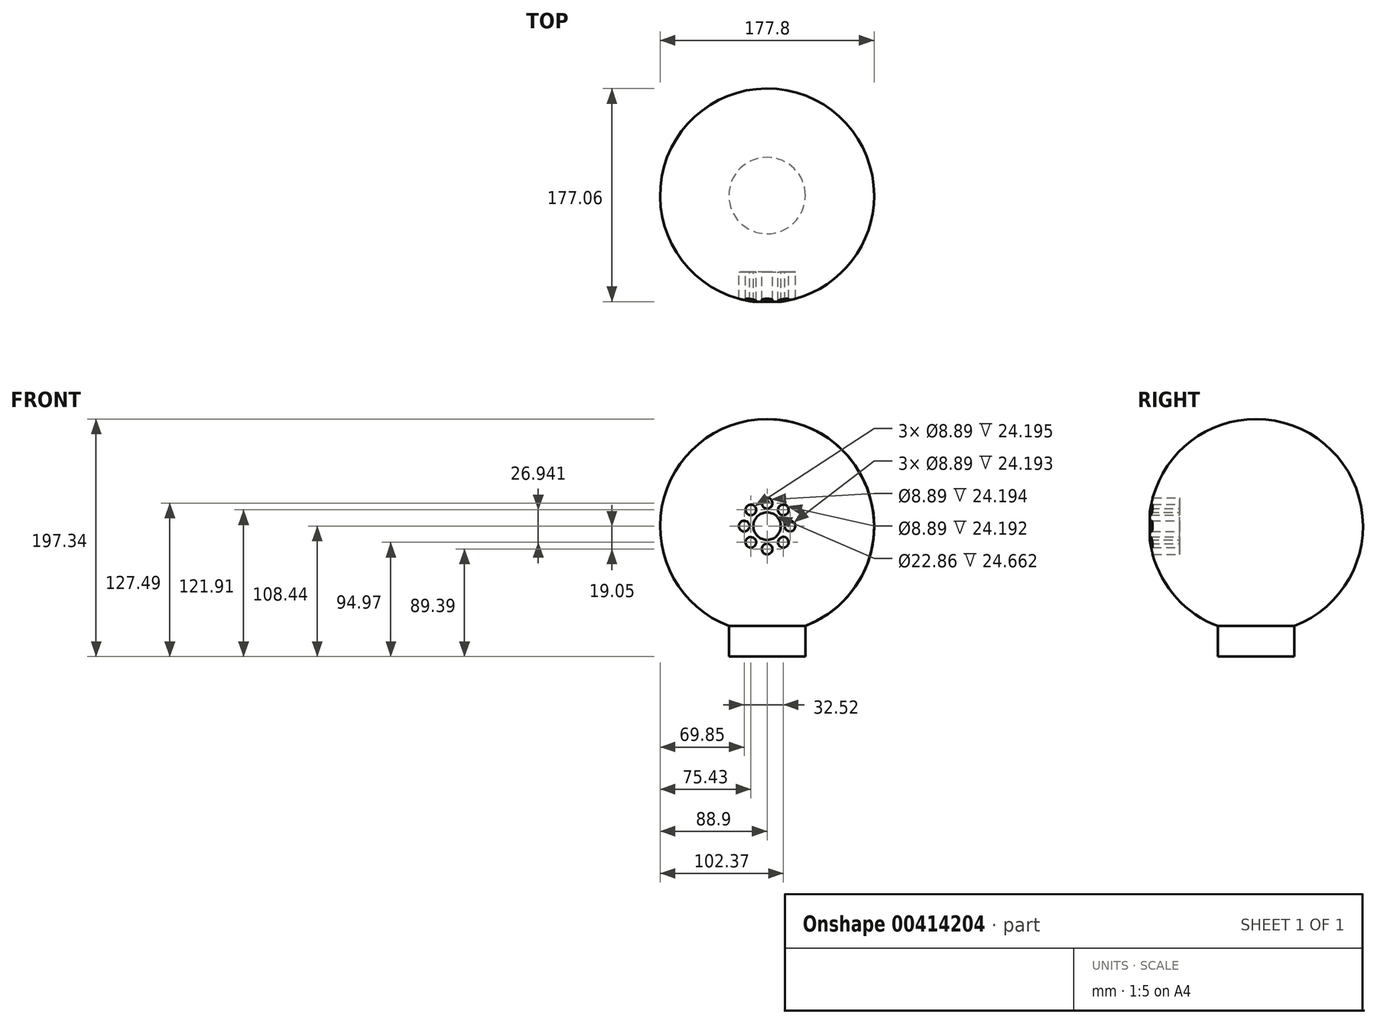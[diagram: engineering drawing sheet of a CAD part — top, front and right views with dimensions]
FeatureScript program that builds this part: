
annotation { "Feature Type Name" : "Feature", "Feature Type Description" : "" }
export const myFeature = defineFeature(function(context is Context, id is Id, definition is map)
    precondition{}
    {
        {
            var Q0;
            Q0=qCreatedBy(makeId("Front.planeOp"),FACE);
            var sketch = newSketch(context, id + "F0", { "sketchPlane" : qUnion([Q0])});
            skArc(sketch, "E0", {"start": v(31.75, -83.04) * mm, "mid": v(87.42, 16.14) * mm, "end": v(0, 88.9) * mm});
            skLineSegment(sketch, "E1", {"start": v(0, 88.9) * mm, "end": v(0, -83.04) * mm});
            skLineSegment(sketch, "E2", {"start": v(31.75, -83.04) * mm, "end": v(31.75, -108.44) * mm});
            skLineSegment(sketch, "E3", {"start": v(31.75, -108.44) * mm, "end": v(0, -108.44) * mm});
            skLineSegment(sketch, "E4", {"start": v(0, -108.44) * mm, "end": v(0, -83.04) * mm});
            skLineSegment(sketch, "E5", {"start": v(0, -83.04) * mm, "end": v(31.75, -83.04) * mm, "construction": true});
            skSolve(sketch);
        }
        {
            var Q0;
            Q0=makeQuery(id+"F0.imprint","IMPRINT",FACE,{"disambiguationData":[TD([[makeQuery(id+"F0.imprint","IMPRINT",EDGE,{"derivedFrom":sQuery(id+"F0.wireOp",EDGE,"E0")}),1.0]])]});
            var Q1;
            Q1=sQuery(id+"F0.wireOp",EDGE,"E1");
            revolve(context, id + "F1", {"entities" : qUnion([Q0]), "axis" : qUnion([Q1]), "revolveType" : RevolveType.FULL});
        }
        {
            var Q0;
            Q0=qCreatedBy(makeId("Front.planeOp"),FACE);
            cPlane(context, id + "F2", {"entities" : qUnion([Q0]), "cplaneType" : CPlaneType.OFFSET, "offset" : 63.5 * mm, "width" : 152.4 * mm, "height" : 152.4 * mm});
        }
        {
            var Q0;
            Q0=qCreatedBy(id+"F2.planeOp",FACE);
            var sketch = newSketch(context, id + "F3", { "sketchPlane" : qUnion([Q0])});
            skCircle(sketch, "E6", {"center": v(0, 0) * mm, "radius": 11.43 * mm});
            skCircle(sketch, "E7", {"center": v(0, 19.05) * mm, "radius": 4.45 * mm});
            skCircle(sketch, "E8", {"center": v(0, -19.05) * mm, "radius": 4.45 * mm});
            skCircle(sketch, "E9", {"center": v(19.05, 0) * mm, "radius": 4.45 * mm});
            skCircle(sketch, "E10", {"center": v(-19.05, 0) * mm, "radius": 4.45 * mm});
            skCircle(sketch, "E11", {"center": v(0, 0) * mm, "radius": 19.05 * mm, "construction": true});
            skCircle(sketch, "E12", {"center": v(-13.47, 13.47) * mm, "radius": 4.45 * mm});
            skCircle(sketch, "E13", {"center": v(13.47, 13.47) * mm, "radius": 4.45 * mm});
            skCircle(sketch, "E14", {"center": v(13.47, -13.47) * mm, "radius": 4.45 * mm});
            skCircle(sketch, "E15", {"center": v(-13.47, -13.47) * mm, "radius": 4.45 * mm});
            skLineSegment(sketch, "E16", {"start": v(0, 0) * mm, "end": v(0, 19.05) * mm, "construction": true});
            skLineSegment(sketch, "E17", {"start": v(0, 0) * mm, "end": v(19.05, 0) * mm});
            skLineSegment(sketch, "E18", {"start": v(0, 0) * mm, "end": v(13.47, -13.47) * mm, "construction": true});
            skLineSegment(sketch, "E19", {"start": v(0, 0) * mm, "end": v(13.47, 13.47) * mm, "construction": true});
            skLineSegment(sketch, "E20", {"start": v(0, 0) * mm, "end": v(-13.47, 13.47) * mm, "construction": true});
            skLineSegment(sketch, "E21", {"start": v(0, 0) * mm, "end": v(-13.47, -13.47) * mm, "construction": true});
            skLineSegment(sketch, "E22", {"start": v(0, 0) * mm, "end": v(0, -19.05) * mm, "construction": true});
            skLineSegment(sketch, "E23", {"start": v(0, 0) * mm, "end": v(-19.05, 0) * mm});
            skSolve(sketch);
        }
        {
            var Q0;
            Q0 = qSketchRegion(id + "F3", true);
            extrude(context, id + "F4", {"entities" : qUnion([Q0]), "operationType" : NewBodyOperationType.REMOVE, "depth" : 76.2 * mm});
        }
    });
